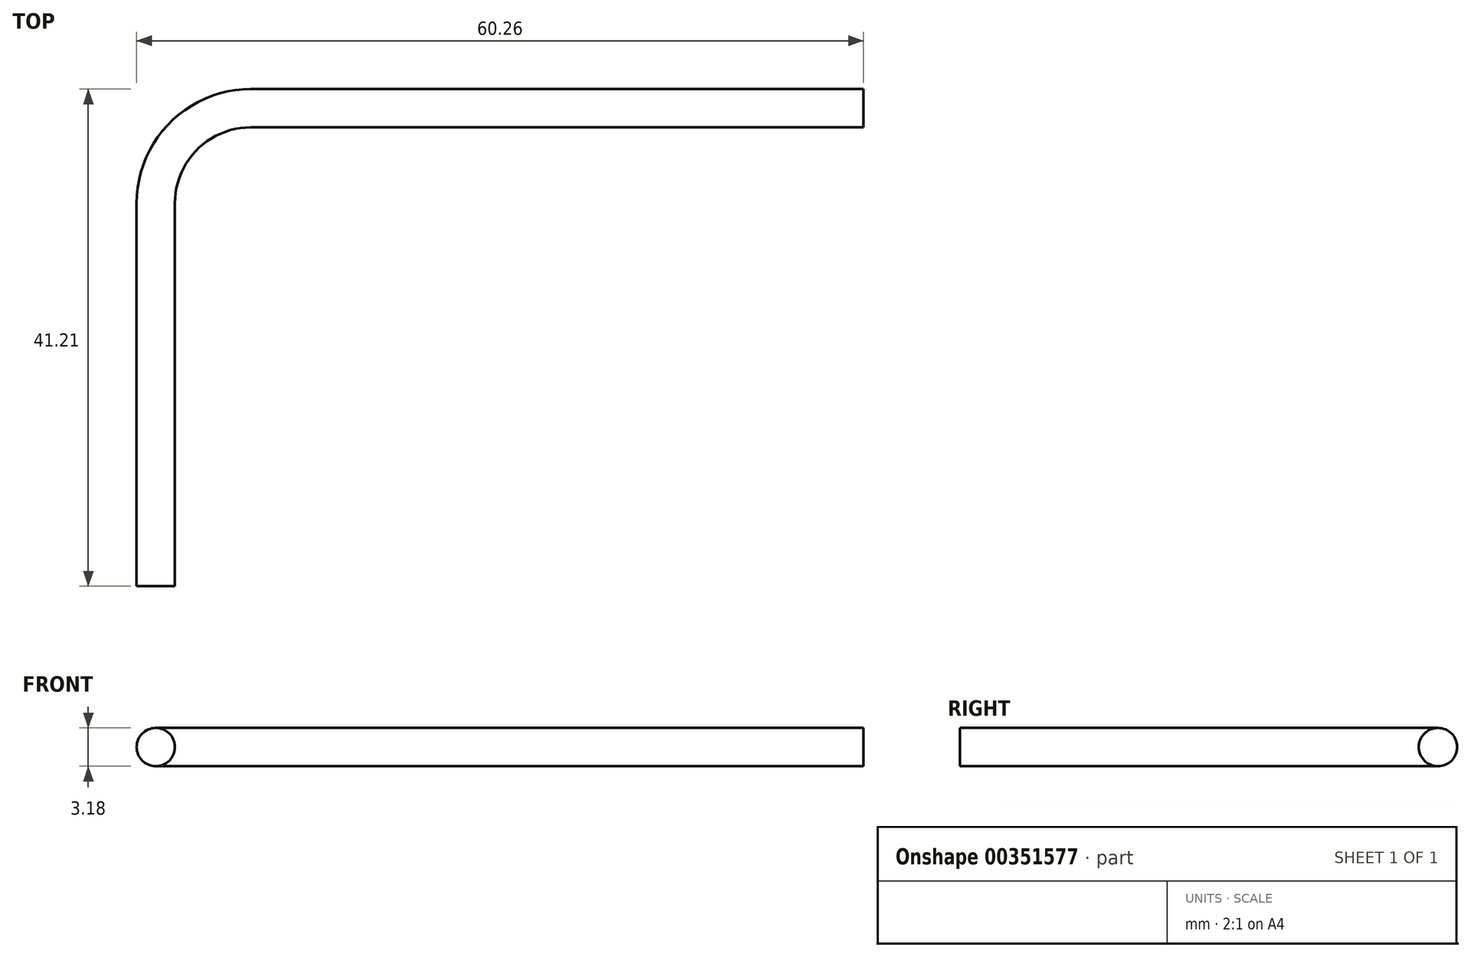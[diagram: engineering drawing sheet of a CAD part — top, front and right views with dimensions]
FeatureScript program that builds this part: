
annotation { "Feature Type Name" : "Feature", "Feature Type Description" : "" }
export const myFeature = defineFeature(function(context is Context, id is Id, definition is map)
    precondition{}
    {
        {
            var Q0;
            Q0=qCreatedBy(makeId("Top.planeOp"),FACE);
            var sketch = newSketch(context, id + "F0", { "sketchPlane" : qUnion([Q0])});
            skLineSegment(sketch, "E0", {"start": v(7.87, 39.62) * mm, "end": v(58.67, 39.62) * mm});
            skPoint(sketch, "E1.center.orphan", {"position": v(7.87, 31.75) * mm});
            skArc(sketch, "E2", {"start": v(7.87, 39.62) * mm, "mid": v(2.3, 37.32) * mm, "end": v(0, 31.75) * mm});
            skLineSegment(sketch, "E3", {"start": v(0, 31.75) * mm, "end": v(0, 0) * mm});
            skSolve(sketch);
        }
        {
            var Q0;
            Q0=qCreatedBy(makeId("Front.planeOp"),FACE);
            var sketch = newSketch(context, id + "F1", { "sketchPlane" : qUnion([Q0])});
            skCircle(sketch, "E4", {"center": v(0, 0) * mm, "radius": 1.59 * mm});
            skSolve(sketch);
        }
        {
            var Q0;
            Q0 = qSketchRegion(id + "F1", true);
            var Q1;
            Q1 = qConstructionFilter(qBodyType(qCreatedBy(id + "F0" ,EDGE), BodyType.WIRE), ConstructionObject.NO);
            sweep(context, id + "F2", {"profiles" : qUnion([Q0]), "path" : qUnion([Q1])});
        }
    });
